# Revit family: Robe_Hook-Grohe-40511001
name_source: partatom
category: Specialty Equipment
revit_build: Autodesk Revit 2018 (Build: 20170223_1515(x64)
units: mm (PartAtom-declared; Revit-internal decimal feet)

## family parameters
Cut with Voids When Loaded = No
Host = Face
OmniClass Number = 23.40.20.21.31
OmniClass Title = Robe Hooks
Part Type = Normal
Room Calculation Point = No
Round Connector Dimension = Use Diameter
Shared = Yes

## types (1)
- 40511001
    Assembly Code = C1030220
    Body Material = Metal-Grohe-001-Starlight Chrome
    Default Elevation = 0"
    Description = ESSENTIALS CUBE Robe Hook
    Height = 1 1/2"
    Installation Type = Wall Mounted
    Length = 2 1/2"
    Manufacturer = Grohe
    Material = Metal-Grohe-001-Starlight Chrome
    Model = 40511001
    Price = Prices may vary. Please consult Manufacturer Representative for most up-to-date price list.
    Product Documentation Link = https://americanstandard.box.com
    Product Page URL = https://www.grohe.us
    Region = North America
    URL = https://www.grohe.us
    Warranty Information = Limited Lifetime Warranty
    Width = 1 1/2"

## geometry (parser evidence)
native form markers: Sweep x3
no freeform markers — native parametric forms only
